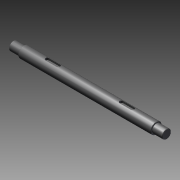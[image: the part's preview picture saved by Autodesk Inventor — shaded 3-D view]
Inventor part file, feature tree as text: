
AUTODESK INVENTOR PART (.ipt)
format: ipt  version: 2011 SP1 (Build 150282100, 282)  size: 131,072 bytes
history: native  units: mm
features: extrude x2, revolve x1, sketch x1
ambient origin geometry x8: Origin, YZ Plane, XZ Plane, XY Plane, X Axis, Y Axis, Z Axis, Center Point
bodies: Solid1 (feature_tree)
feature tree (4):
  revolve  "Revolution1"  [1 undecoded]
  extrude  "Extrusion1"  Depth=3.0mm TaperAngle=0.0deg
  extrude  "Extrusion2"  [1 undecoded]
  sketch  "Sketch_1"  dims[d0=360.0deg d1=3.0mm d2=0.0mm d3=3.0mm d4=0.0mm]
note: 2 required parameter values undecoded (feature->parameter linkage not recoverable at this tier; creation-order binding heuristic only, values carry confidence <= 0.55)